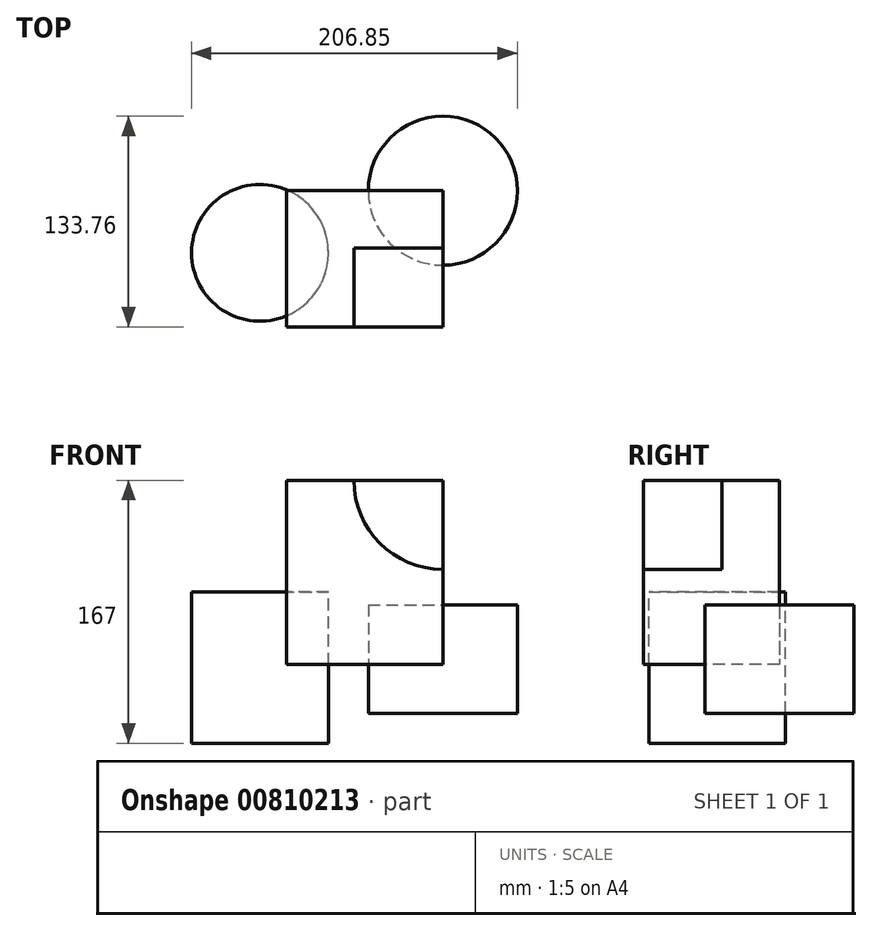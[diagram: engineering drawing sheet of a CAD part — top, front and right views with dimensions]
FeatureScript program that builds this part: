
annotation { "Feature Type Name" : "Feature", "Feature Type Description" : "" }
export const myFeature = defineFeature(function(context is Context, id is Id, definition is map)
    precondition{}
    {
        {
            var Q0;
            Q0=qCreatedBy(makeId("Top.planeOp"),FACE);
            var sketch = newSketch(context, id + "F0", { "sketchPlane" : qUnion([Q0])});
            skLineSegment(sketch, "E0.bottom", {"start": v(49.55, 43.22) * mm, "end": v(-49.55, 43.22) * mm});
            skLineSegment(sketch, "E0.top", {"start": v(49.55, -43.22) * mm, "end": v(-49.55, -43.22) * mm});
            skLineSegment(sketch, "E0.left", {"start": v(49.55, 43.22) * mm, "end": v(49.55, -43.22) * mm});
            skLineSegment(sketch, "E0.right", {"start": v(-49.55, 43.22) * mm, "end": v(-49.55, -43.22) * mm});
            skPoint(sketch, "E0.middle", {"position": v(0, 0) * mm});
            skSolve(sketch);
        }
        {
            var Q0;
            Q0 = qSketchRegion(id + "F0", true);
            extrude(context, id + "F1", {"entities" : qUnion([Q0]), "depth" : 117 * mm, "offsetDistance" : 25 * mm});
        }
        {
            var Q0;
            Q0=makeQuery(id+"F1.opExtrude","SWEPT_FACE",FACE,{"disambiguationData":[OSD([sQuery(id+"F0.wireOp",EDGE,"E0.top")])]});
            var sketch = newSketch(context, id + "F2", { "sketchPlane" : qUnion([Q0])});
            skCircle(sketch, "E1", {"center": v(49.55, 117) * mm, "radius": 56.48 * mm});
            skSolve(sketch);
        }
        {
            var Q0;
            Q0 = qSketchRegion(id + "F2", true);
            extrude(context, id + "F3", {"entities" : qUnion([Q0]), "operationType" : NewBodyOperationType.REMOVE, "oppositeDirection" : true, "depth" : 50 * mm, "offsetDistance" : 25 * mm});
        }
        {
            var Q0;
            Q0=makeQuery(id+"F1.opExtrude","CAP_FACE",FACE,{"disambiguationData":[OSD([sQuery(id+"F0.wireOp",EDGE,"E0.bottom"),sQuery(id+"F0.wireOp",EDGE,"E0.top"),sQuery(id+"F0.wireOp",EDGE,"E0.left"),sQuery(id+"F0.wireOp",EDGE,"E0.right")])],"isStart":true});
            var sketch = newSketch(context, id + "F4", { "sketchPlane" : qUnion([Q0])});
            skCircle(sketch, "E2", {"center": v(-49.55, 43.22) * mm, "radius": 43.43 * mm});
            skSolve(sketch);
        }
        {
            var Q0;
            Q0 = qSketchRegion(id + "F4", true);
            extrude(context, id + "F5", {"entities" : qUnion([Q0]), "depth" : 56 * mm, "offsetDistance" : 25 * mm, "hasSecondDirection" : true, "secondDirectionOppositeDirection" : true, "secondDirectionDepth" : 40 * mm});
        }
        {
            var Q0;
            Q0=makeQuery(id+"F1.opExtrude","CAP_FACE",FACE,{"disambiguationData":[OSD([sQuery(id+"F0.wireOp",EDGE,"E0.bottom"),sQuery(id+"F0.wireOp",EDGE,"E0.top"),sQuery(id+"F0.wireOp",EDGE,"E0.left"),sQuery(id+"F0.wireOp",EDGE,"E0.right")])],"isStart":true});
            var sketch = newSketch(context, id + "F6", { "sketchPlane" : qUnion([Q0])});
            skCircle(sketch, "E3", {"center": v(49.55, -43.22) * mm, "radius": 47.32 * mm});
            skSolve(sketch);
        }
        {
            var Q0;
            Q0 = qSketchRegion(id + "F6", true);
            extrude(context, id + "F7", {"entities" : qUnion([Q0]), "operationType" : NewBodyOperationType.ADD, "oppositeDirection" : true, "depth" : 38 * mm, "offsetDistance" : 25 * mm, "hasSecondDirection" : true, "secondDirectionOppositeDirection" : false, "secondDirectionDepth" : 31 * mm});
        }
        {
            var Q0;
            Q0=makeQuery(id+"F5.opExtrude","SWEPT_BODY",BODY,{"disambiguationData":[OSD([sQuery(id+"F4.wireOp",EDGE,"E2")])]});
            transform(context, id + "F8", {"entities" : qUnion([Q0]), "transformType" : TransformType.TRANSLATION_3D, "dx" : -17 * mm, "dy" : 47 * mm, "dz" : 6 * mm, "makeCopy" : false});
        }
    });
